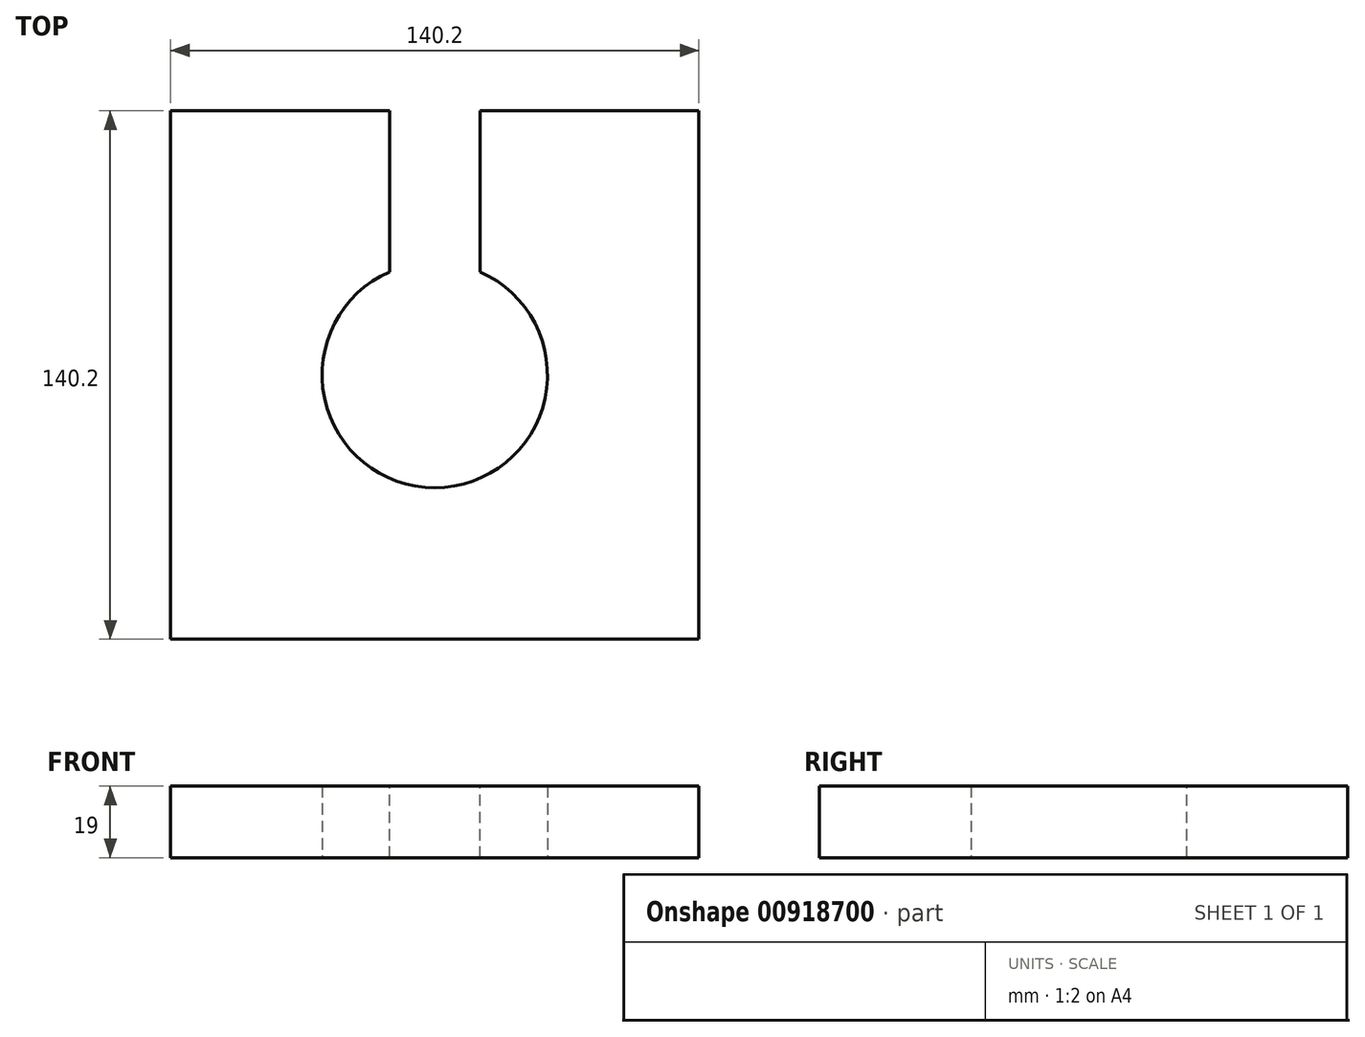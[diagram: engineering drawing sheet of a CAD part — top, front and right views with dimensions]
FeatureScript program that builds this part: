
annotation { "Feature Type Name" : "Feature", "Feature Type Description" : "" }
export const myFeature = defineFeature(function(context is Context, id is Id, definition is map)
    precondition{}
    {
        {
            var Q0;
            Q0=qCreatedBy(makeId("Top.planeOp"),FACE);
            var sketch = newSketch(context, id + "F0", { "sketchPlane" : qUnion([Q0])});
            skLineSegment(sketch, "E0.bottom", {"start": v(70.1, -70.1) * mm, "end": v(-70.1, -70.1) * mm});
            skLineSegment(sketch, "E0.top", {"start": v(70.1, 70.1) * mm, "end": v(-70.1, 70.1) * mm});
            skLineSegment(sketch, "E0.left", {"start": v(70.1, -70.1) * mm, "end": v(70.1, 70.1) * mm});
            skLineSegment(sketch, "E0.right", {"start": v(-70.1, -70.1) * mm, "end": v(-70.1, 70.1) * mm});
            skPoint(sketch, "E0.middle", {"position": v(0, 0) * mm});
            skCircle(sketch, "E1", {"center": v(0, 0) * mm, "radius": 29.9 * mm});
            skSolve(sketch);
        }
        {
            var Q0;
            Q0=makeQuery(id+"F0.imprint","IMPRINT",FACE,{"disambiguationData":[TD([[makeQuery(id+"F0.imprint","IMPRINT",EDGE,{"derivedFrom":sQuery(id+"F0.wireOp",EDGE,"E0.bottom")}),-1.0]])]});
            extrude(context, id + "F1", {"entities" : qUnion([Q0]), "depth" : 19 * mm, "offsetDistance" : 25 * mm});
        }
        {
            var Q0;
            Q0=makeQuery(id+"F1.opExtrude","CAP_FACE",FACE,{"disambiguationData":[OSD([sQuery(id+"F0.wireOp",EDGE,"E0.bottom"),sQuery(id+"F0.wireOp",EDGE,"E0.top"),sQuery(id+"F0.wireOp",EDGE,"E0.left"),sQuery(id+"F0.wireOp",EDGE,"E0.right"),sQuery(id+"F0.wireOp",EDGE,"E1")])],"isStart":false});
            var sketch = newSketch(context, id + "F2", { "sketchPlane" : qUnion([Q0])});
            skLineSegment(sketch, "E2.bottom", {"start": v(-12, 70.1) * mm, "end": v(12, 70.1) * mm});
            skLineSegment(sketch, "E2.top", {"start": v(-12, -70.1) * mm, "end": v(12, -70.1) * mm});
            skLineSegment(sketch, "E2.left", {"start": v(-12, 70.1) * mm, "end": v(-12, -70.1) * mm});
            skLineSegment(sketch, "E2.right", {"start": v(12, 70.1) * mm, "end": v(12, -70.1) * mm});
            skLineSegment(sketch, "E3", {"start": v(0, 70.1) * mm, "end": v(0, -70.1) * mm, "construction": true});
            skSolve(sketch);
        }
        {
            var Q0;
            {var subQ0=sQuery(id+"F2.wireOp",EDGE,"E2.bottom");Q0=makeQuery(id+"F2.imprint","IMPRINT",FACE,{"disambiguationData":[TD([[makeQuery(id+"F2.imprint","IMPRINT",EDGE,{"derivedFrom":subQ0}),1.0]])]});}
            extrude(context, id + "F3", {"entities" : qUnion([Q0]), "operationType" : NewBodyOperationType.REMOVE, "oppositeDirection" : true, "depth" : 19 * mm, "offsetDistance" : 25 * mm});
        }
    });
